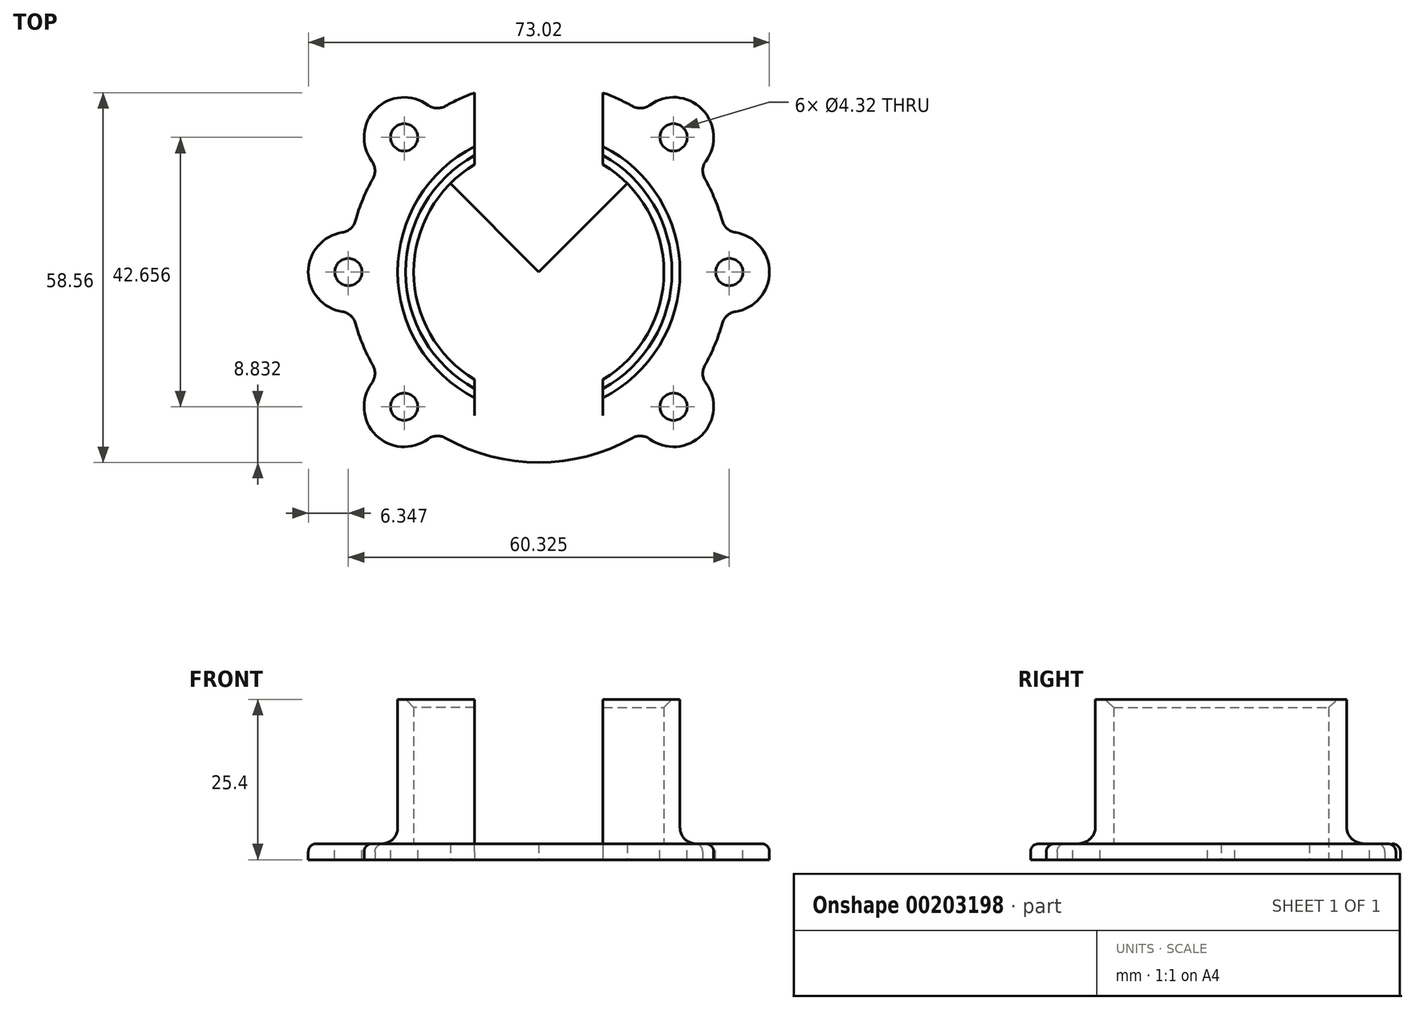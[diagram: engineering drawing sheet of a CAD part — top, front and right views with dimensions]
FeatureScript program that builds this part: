
annotation { "Feature Type Name" : "Feature", "Feature Type Description" : "" }
export const myFeature = defineFeature(function(context is Context, id is Id, definition is map)
    precondition{}
    {
        {
            var Q0;
            Q0=qCreatedBy(makeId("Top.planeOp"),FACE);
            var sketch = newSketch(context, id + "F0", { "sketchPlane" : qUnion([Q0])});
            skArc(sketch, "E0", {"start": v(-10.16, 17) * mm, "mid": v(-19.81, 0) * mm, "end": v(-10.16, -17) * mm});
            skArc(sketch, "E1.0", {"start": v(-10.16, 19.9) * mm, "mid": v(-22.35, 0) * mm, "end": v(-10.16, -19.9) * mm});
            skArc(sketch, "E2", {"start": v(-10.16, -36.72) * mm, "mid": v(0, -38.1) * mm, "end": v(10.16, -36.72) * mm});
            skArc(sketch, "E3", {"start": v(-26.28, 14.81) * mm, "mid": v(-27.87, 11.54) * mm, "end": v(-29.05, 8.1) * mm});
            skLineSegment(sketch, "E4", {"start": v(0, 0) * mm, "end": v(0, 38.1) * mm});
            skLineSegment(sketch, "E5", {"start": v(0, 38.1) * mm, "end": v(-10.16, 38.1) * mm});
            skLineSegment(sketch, "E6", {"start": v(-10.16, 38.1) * mm, "end": v(-10.16, 17) * mm});
            skLineSegment(sketch, "E7.MirrorCS", {"start": v(10.16, 38.1) * mm, "end": v(10.16, 17) * mm});
            skLineSegment(sketch, "E8.MirrorCS", {"start": v(0, 38.1) * mm, "end": v(10.16, 38.1) * mm});
            skLineSegment(sketch, "E9.MirrorCS", {"start": v(-10.16, -38.1) * mm, "end": v(-10.16, -17) * mm});
            skLineSegment(sketch, "E10.MirrorCS", {"start": v(10.16, -38.1) * mm, "end": v(10.16, -17) * mm});
            skArc(sketch, "E11.trimOffspring", {"start": v(10.16, -19.9) * mm, "mid": v(22.35, 0) * mm, "end": v(10.16, 19.9) * mm});
            skArc(sketch, "E12.trimOffspring", {"start": v(10.16, -17) * mm, "mid": v(19.81, 0) * mm, "end": v(10.16, 17) * mm});
            skLineSegment(sketch, "E13", {"start": v(-10.16, -38.1) * mm, "end": v(10.16, -38.1) * mm});
            skLineSegment(sketch, "E14", {"start": v(0, 0) * mm, "end": v(-30.16, 0) * mm});
            skLineSegment(sketch, "E15.1.0", {"start": v(0, 0) * mm, "end": v(-21.33, -21.33) * mm});
            skLineSegment(sketch, "E15.2.0", {"start": v(0, 0) * mm, "end": v(0, -30.16) * mm});
            skLineSegment(sketch, "E15.3.0", {"start": v(0, 0) * mm, "end": v(21.33, -21.33) * mm});
            skLineSegment(sketch, "E15.4.0", {"start": v(0, 0) * mm, "end": v(30.16, 0) * mm});
            skLineSegment(sketch, "E15.5.0", {"start": v(0, 0) * mm, "end": v(21.33, 21.33) * mm});
            skLineSegment(sketch, "E15.6.0", {"start": v(0, 0) * mm, "end": v(0, 30.16) * mm});
            skLineSegment(sketch, "E15.7.0", {"start": v(0, 0) * mm, "end": v(-21.33, 21.33) * mm});
            skArc(sketch, "E16", {"start": v(-31.12, 6.28) * mm, "mid": v(-36.51, 0) * mm, "end": v(-31.12, -6.28) * mm});
            skArc(sketch, "E17.1.0", {"start": v(-26.44, -17.56) * mm, "mid": v(-25.82, -25.82) * mm, "end": v(-17.56, -26.44) * mm});
            skArc(sketch, "E17.3.0", {"start": v(17.56, -26.44) * mm, "mid": v(25.82, -25.82) * mm, "end": v(26.44, -17.56) * mm});
            skArc(sketch, "E17.4.0", {"start": v(31.12, -6.28) * mm, "mid": v(36.51, 0) * mm, "end": v(31.12, 6.28) * mm});
            skArc(sketch, "E17.5.0", {"start": v(26.44, 17.56) * mm, "mid": v(25.82, 25.82) * mm, "end": v(17.56, 26.44) * mm});
            skArc(sketch, "E17.7.0", {"start": v(-17.56, 26.44) * mm, "mid": v(-25.82, 25.82) * mm, "end": v(-26.44, 17.56) * mm});
            skArc(sketch, "E18.trimOffspring", {"start": v(10.16, 36.72) * mm, "mid": v(0, 38.1) * mm, "end": v(-10.16, 36.72) * mm});
            skArc(sketch, "E19.trimOffspring", {"start": v(-29.05, -8.1) * mm, "mid": v(-27.87, -11.54) * mm, "end": v(-26.28, -14.81) * mm});
            skArc(sketch, "E20.trimOffspring", {"start": v(-14.81, -26.28) * mm, "mid": v(0, -30.16) * mm, "end": v(14.81, -26.28) * mm});
            skArc(sketch, "E21.trimOffspring", {"start": v(26.28, -14.81) * mm, "mid": v(27.87, -11.54) * mm, "end": v(29.05, -8.1) * mm});
            skArc(sketch, "E22.trimOffspring", {"start": v(29.05, 8.1) * mm, "mid": v(27.87, 11.54) * mm, "end": v(26.28, 14.81) * mm});
            skArc(sketch, "E23.trimOffspring", {"start": v(14.81, 26.28) * mm, "mid": v(0, 30.16) * mm, "end": v(-14.81, 26.28) * mm});
            skPoint(sketch, "E24.visualSharp", {"position": v(-16.4, 25.32) * mm});
            skArc(sketch, "E24.filletArc", {"start": v(-17.56, 26.44) * mm, "mid": v(-16.21, 25.95) * mm, "end": v(-14.81, 26.28) * mm});
            skPoint(sketch, "E25.visualSharp", {"position": v(-25.32, 16.4) * mm});
            skArc(sketch, "E25.filletArc", {"start": v(-26.28, 14.81) * mm, "mid": v(-25.95, 16.21) * mm, "end": v(-26.44, 17.56) * mm});
            skPoint(sketch, "E26.visualSharp", {"position": v(-29.5, 6.31) * mm});
            skArc(sketch, "E26.filletArc", {"start": v(-31.12, 6.28) * mm, "mid": v(-29.82, 6.89) * mm, "end": v(-29.05, 8.1) * mm});
            skPoint(sketch, "E27.visualSharp", {"position": v(-29.5, -6.31) * mm});
            skArc(sketch, "E27.filletArc", {"start": v(-29.05, -8.1) * mm, "mid": v(-29.82, -6.89) * mm, "end": v(-31.12, -6.28) * mm});
            skPoint(sketch, "E28.visualSharp", {"position": v(-25.32, -16.4) * mm});
            skArc(sketch, "E28.filletArc", {"start": v(-26.44, -17.56) * mm, "mid": v(-25.95, -16.21) * mm, "end": v(-26.28, -14.81) * mm});
            skPoint(sketch, "E29.visualSharp", {"position": v(-16.4, -25.32) * mm});
            skArc(sketch, "E29.filletArc", {"start": v(-14.81, -26.28) * mm, "mid": v(-16.21, -25.95) * mm, "end": v(-17.56, -26.44) * mm});
            skPoint(sketch, "E30.visualSharp", {"position": v(16.4, -25.32) * mm});
            skArc(sketch, "E30.filletArc", {"start": v(17.56, -26.44) * mm, "mid": v(16.21, -25.95) * mm, "end": v(14.81, -26.28) * mm});
            skPoint(sketch, "E31.visualSharp", {"position": v(25.32, -16.4) * mm});
            skArc(sketch, "E31.filletArc", {"start": v(26.28, -14.81) * mm, "mid": v(25.95, -16.21) * mm, "end": v(26.44, -17.56) * mm});
            skPoint(sketch, "E32.visualSharp", {"position": v(29.5, -6.31) * mm});
            skArc(sketch, "E32.filletArc", {"start": v(31.12, -6.28) * mm, "mid": v(29.82, -6.89) * mm, "end": v(29.05, -8.1) * mm});
            skPoint(sketch, "E33.visualSharp", {"position": v(29.5, 6.31) * mm});
            skArc(sketch, "E33.filletArc", {"start": v(29.05, 8.1) * mm, "mid": v(29.82, 6.89) * mm, "end": v(31.12, 6.28) * mm});
            skPoint(sketch, "E34.visualSharp", {"position": v(25.32, 16.4) * mm});
            skArc(sketch, "E34.filletArc", {"start": v(26.44, 17.56) * mm, "mid": v(25.95, 16.21) * mm, "end": v(26.28, 14.81) * mm});
            skPoint(sketch, "E35.visualSharp", {"position": v(16.4, 25.32) * mm});
            skArc(sketch, "E35.filletArc", {"start": v(14.81, 26.28) * mm, "mid": v(16.21, 25.95) * mm, "end": v(17.56, 26.44) * mm});
            skSolve(sketch);
        }
        {
            var Q0;
            {var subQ0=sQuery(id+"F0.wireOp",EDGE,"E15.6.0");Q0=makeQuery(id+"F0.imprint","IMPRINT",FACE,{"disambiguationData":[TD([[makeQuery(id+"F0.imprint","IMPRINT",EDGE,{"derivedFrom":subQ0}),1.0]])]});}
            var Q1;
            {var subQ0=sQuery(id+"F0.wireOp",EDGE,"E15.6.0");Q1=makeQuery(id+"F0.imprint","IMPRINT",FACE,{"disambiguationData":[TD([[makeQuery(id+"F0.imprint","IMPRINT",EDGE,{"derivedFrom":subQ0}),-1.0]])]});}
            var Q2;
            Q2=makeQuery(id+"F0.imprint","IMPRINT",FACE,{"disambiguationData":[TD([[makeQuery(id+"F0.imprint","IMPRINT",EDGE,{"derivedFrom":sQuery(id+"F0.wireOp",EDGE,"E17.3.0")}),1.0]])]});
            var Q3;
            Q3=makeQuery(id+"F0.imprint","IMPRINT",FACE,{"disambiguationData":[TD([[makeQuery(id+"F0.imprint","IMPRINT",EDGE,{"derivedFrom":sQuery(id+"F0.wireOp",EDGE,"E3")}),1.0]])]});
            var Q4;
            {var subQ0=sQuery(id+"F0.wireOp",EDGE,"E6");var subQ1=sQuery(id+"F0.wireOp",EDGE,"E0");var subQ2=makeQuery(id+"F0.imprint","INTERSECT",VERTEX,{"derivedFrom":[subQ1,subQ0]});Q4=makeQuery(id+"F0.imprint","IMPRINT",FACE,{"disambiguationData":[TD([[makeQuery(id+"F0.imprint","IMPRINT",EDGE,{"disambiguationData":[TD([[subQ2,-1.0]])],"derivedFrom":subQ1}),-1.0]])]});}
            var Q5;
            {var subQ0=sQuery(id+"F0.wireOp",EDGE,"E12.trimOffspring");var subQ1=sQuery(id+"F0.wireOp",EDGE,"E7.MirrorCS");var subQ2=makeQuery(id+"F0.imprint","INTERSECT",VERTEX,{"derivedFrom":[subQ1,subQ0]});Q5=makeQuery(id+"F0.imprint","IMPRINT",FACE,{"disambiguationData":[TD([[makeQuery(id+"F0.imprint","IMPRINT",EDGE,{"disambiguationData":[TD([[subQ2,1.0]])],"derivedFrom":subQ1}),1.0]])]});}
            var Q6;
            {var subQ0=sQuery(id+"F0.wireOp",EDGE,"E15.7.0");var subQ1=sQuery(id+"F0.wireOp",EDGE,"E0");var subQ2=makeQuery(id+"F0.imprint","INTERSECT",VERTEX,{"derivedFrom":[subQ1,subQ0]});Q6=makeQuery(id+"F0.imprint","IMPRINT",FACE,{"disambiguationData":[TD([[makeQuery(id+"F0.imprint","IMPRINT",EDGE,{"disambiguationData":[TD([[subQ2,-1.0]])],"derivedFrom":subQ1}),-1.0]])]});}
            var Q7;
            {var subQ0=sQuery(id+"F0.wireOp",EDGE,"E15.7.0");var subQ1=sQuery(id+"F0.wireOp",EDGE,"E0");var subQ2=makeQuery(id+"F0.imprint","INTERSECT",VERTEX,{"derivedFrom":[subQ1,subQ0]});Q7=makeQuery(id+"F0.imprint","IMPRINT",FACE,{"disambiguationData":[TD([[makeQuery(id+"F0.imprint","IMPRINT",EDGE,{"disambiguationData":[TD([[subQ2,-1.0]])],"derivedFrom":subQ1}),1.0]])]});}
            var Q8;
            {var subQ0=sQuery(id+"F0.wireOp",EDGE,"E14");var subQ1=sQuery(id+"F0.wireOp",EDGE,"E0");var subQ2=makeQuery(id+"F0.imprint","INTERSECT",VERTEX,{"derivedFrom":[subQ1,subQ0]});Q8=makeQuery(id+"F0.imprint","IMPRINT",FACE,{"disambiguationData":[TD([[makeQuery(id+"F0.imprint","IMPRINT",EDGE,{"disambiguationData":[TD([[subQ2,-1.0]])],"derivedFrom":subQ1}),-1.0]])]});}
            var Q9;
            {var subQ0=sQuery(id+"F0.wireOp",EDGE,"E14");var subQ1=sQuery(id+"F0.wireOp",EDGE,"E0");var subQ2=makeQuery(id+"F0.imprint","INTERSECT",VERTEX,{"derivedFrom":[subQ1,subQ0]});Q9=makeQuery(id+"F0.imprint","IMPRINT",FACE,{"disambiguationData":[TD([[makeQuery(id+"F0.imprint","IMPRINT",EDGE,{"disambiguationData":[TD([[subQ2,-1.0]])],"derivedFrom":subQ1}),1.0]])]});}
            var Q10;
            {var subQ0=sQuery(id+"F0.wireOp",EDGE,"E15.2.0");Q10=makeQuery(id+"F0.imprint","IMPRINT",FACE,{"disambiguationData":[TD([[makeQuery(id+"F0.imprint","IMPRINT",EDGE,{"derivedFrom":subQ0}),-1.0]])]});}
            var Q11;
            {var subQ6=sQuery(id+"F0.wireOp",EDGE,"E15.2.0");Q11=makeQuery(id+"F0.imprint","IMPRINT",FACE,{"disambiguationData":[TD([[makeQuery(id+"F0.imprint","IMPRINT",EDGE,{"derivedFrom":subQ6}),1.0]])]});}
            var Q12;
            {var subQ0=sQuery(id+"F0.wireOp",EDGE,"E15.3.0");var subQ1=sQuery(id+"F0.wireOp",EDGE,"E12.trimOffspring");var subQ2=makeQuery(id+"F0.imprint","INTERSECT",VERTEX,{"derivedFrom":[subQ1,subQ0]});Q12=makeQuery(id+"F0.imprint","IMPRINT",FACE,{"disambiguationData":[TD([[makeQuery(id+"F0.imprint","IMPRINT",EDGE,{"disambiguationData":[TD([[subQ2,-1.0]])],"derivedFrom":subQ1}),1.0]])]});}
            var Q13;
            {var subQ0=sQuery(id+"F0.wireOp",EDGE,"E15.4.0");var subQ1=sQuery(id+"F0.wireOp",EDGE,"E12.trimOffspring");var subQ2=makeQuery(id+"F0.imprint","INTERSECT",VERTEX,{"derivedFrom":[subQ1,subQ0]});Q13=makeQuery(id+"F0.imprint","IMPRINT",FACE,{"disambiguationData":[TD([[makeQuery(id+"F0.imprint","IMPRINT",EDGE,{"disambiguationData":[TD([[subQ2,-1.0]])],"derivedFrom":subQ1}),1.0]])]});}
            var Q14;
            {var subQ0=sQuery(id+"F0.wireOp",EDGE,"E15.4.0");var subQ1=sQuery(id+"F0.wireOp",EDGE,"E11.trimOffspring");var subQ2=makeQuery(id+"F0.imprint","INTERSECT",VERTEX,{"derivedFrom":[subQ1,subQ0]});Q14=makeQuery(id+"F0.imprint","IMPRINT",FACE,{"disambiguationData":[TD([[makeQuery(id+"F0.imprint","IMPRINT",EDGE,{"disambiguationData":[TD([[subQ2,-1.0]])],"derivedFrom":subQ1}),1.0]])]});}
            var Q15;
            {var subQ0=sQuery(id+"F0.wireOp",EDGE,"E15.3.0");var subQ1=sQuery(id+"F0.wireOp",EDGE,"E11.trimOffspring");var subQ2=makeQuery(id+"F0.imprint","INTERSECT",VERTEX,{"derivedFrom":[subQ1,subQ0]});Q15=makeQuery(id+"F0.imprint","IMPRINT",FACE,{"disambiguationData":[TD([[makeQuery(id+"F0.imprint","IMPRINT",EDGE,{"disambiguationData":[TD([[subQ2,-1.0]])],"derivedFrom":subQ1}),1.0]])]});}
            var Q16;
            {var subQ0=sQuery(id+"F0.wireOp",EDGE,"E12.trimOffspring");var subQ1=sQuery(id+"F0.wireOp",EDGE,"E10.MirrorCS");var subQ2=makeQuery(id+"F0.imprint","INTERSECT",VERTEX,{"derivedFrom":[subQ1,subQ0]});Q16=makeQuery(id+"F0.imprint","IMPRINT",FACE,{"disambiguationData":[TD([[makeQuery(id+"F0.imprint","IMPRINT",EDGE,{"disambiguationData":[TD([[subQ2,1.0]])],"derivedFrom":subQ1}),-1.0]])]});}
            var Q17;
            {var subQ0=sQuery(id+"F0.wireOp",EDGE,"E9.MirrorCS");var subQ1=sQuery(id+"F0.wireOp",EDGE,"E0");var subQ2=makeQuery(id+"F0.imprint","INTERSECT",VERTEX,{"derivedFrom":[subQ1,subQ0]});Q17=makeQuery(id+"F0.imprint","IMPRINT",FACE,{"disambiguationData":[TD([[makeQuery(id+"F0.imprint","IMPRINT",EDGE,{"disambiguationData":[TD([[subQ2,1.0]])],"derivedFrom":subQ1}),-1.0]])]});}
            extrude(context, id + "F1", {"entities" : qUnion([Q0, Q1, Q2, Q3, Q4, Q5, Q6, Q7, Q8, Q9, Q10, Q11, Q12, Q13, Q14, Q15, Q16, Q17]), "depth" : 2.54 * mm});
        }
        {
            var Q0;
            Q0=sQuery(id+"F0.wireOp",VERTEX,"E15.7.0.end");
            var Q1;
            Q1=sQuery(id+"F0.wireOp",VERTEX,"E14.end");
            var Q2;
            Q2=sQuery(id+"F0.wireOp",VERTEX,"E15.1.0.end");
            var Q3;
            Q3=sQuery(id+"F0.wireOp",VERTEX,"E17.3.0.center");
            var Q4;
            Q4=sQuery(id+"F0.wireOp",VERTEX,"E15.4.0.end");
            var Q5;
            Q5=sQuery(id+"F0.wireOp",VERTEX,"E15.5.0.end");
            var Q6;
            Q6=makeQuery(id+"F1.opExtrude","SWEPT_BODY",BODY,{"disambiguationData":[OSD([sQuery(id+"F0.wireOp",EDGE,"E3"),sQuery(id+"F0.wireOp",EDGE,"E16"),sQuery(id+"F0.wireOp",EDGE,"E17.1.0"),sQuery(id+"F0.wireOp",EDGE,"E17.3.0"),sQuery(id+"F0.wireOp",EDGE,"E17.4.0"),sQuery(id+"F0.wireOp",EDGE,"E17.5.0"),sQuery(id+"F0.wireOp",EDGE,"E17.7.0"),sQuery(id+"F0.wireOp",EDGE,"E19.trimOffspring"),sQuery(id+"F0.wireOp",EDGE,"E20.trimOffspring"),sQuery(id+"F0.wireOp",EDGE,"E21.trimOffspring"),sQuery(id+"F0.wireOp",EDGE,"E22.trimOffspring"),sQuery(id+"F0.wireOp",EDGE,"E23.trimOffspring"),sQuery(id+"F0.wireOp",EDGE,"E24.filletArc"),sQuery(id+"F0.wireOp",EDGE,"E25.filletArc"),sQuery(id+"F0.wireOp",EDGE,"E26.filletArc"),sQuery(id+"F0.wireOp",EDGE,"E27.filletArc"),sQuery(id+"F0.wireOp",EDGE,"E28.filletArc"),sQuery(id+"F0.wireOp",EDGE,"E29.filletArc"),sQuery(id+"F0.wireOp",EDGE,"E30.filletArc"),sQuery(id+"F0.wireOp",EDGE,"E31.filletArc"),sQuery(id+"F0.wireOp",EDGE,"E32.filletArc"),sQuery(id+"F0.wireOp",EDGE,"E33.filletArc"),sQuery(id+"F0.wireOp",EDGE,"E34.filletArc"),sQuery(id+"F0.wireOp",EDGE,"E35.filletArc")])]});
            hole(context, id + "F2", {"style" : HoleStyle.SIMPLE, "endStyle" : HoleEndStyle.BLIND, "oppositeDirection" : true, "standardTappedOrClearance" : lookupTablePath({ "standard" : "ANSI", "fit" : "Close", "size" : "#8", "type" : "Clearance" }), "standardBlindInLast" : lookupTablePath({ "fit" : "Close", "standard" : "ANSI", "size" : "#8", "type" : "Clearance" }), "holeDiameter" : 4.32 * mm, "holeDepth" : 25.4 * mm, "locations" : qUnion([Q0, Q1, Q2, Q3, Q4, Q5]), "scope" : qUnion([Q6])});
        }
        {
            var Q0;
            {var subQ0=sQuery(id+"F0.wireOp",EDGE,"E6");var subQ1=sQuery(id+"F0.wireOp",EDGE,"E0");var subQ2=makeQuery(id+"F0.imprint","INTERSECT",VERTEX,{"derivedFrom":[subQ1,subQ0]});Q0=makeQuery(id+"F0.imprint","IMPRINT",FACE,{"disambiguationData":[TD([[makeQuery(id+"F0.imprint","IMPRINT",EDGE,{"disambiguationData":[TD([[subQ2,-1.0]])],"derivedFrom":subQ1}),-1.0]])]});}
            var Q1;
            {var subQ0=sQuery(id+"F0.wireOp",EDGE,"E15.7.0");var subQ1=sQuery(id+"F0.wireOp",EDGE,"E0");var subQ2=makeQuery(id+"F0.imprint","INTERSECT",VERTEX,{"derivedFrom":[subQ1,subQ0]});Q1=makeQuery(id+"F0.imprint","IMPRINT",FACE,{"disambiguationData":[TD([[makeQuery(id+"F0.imprint","IMPRINT",EDGE,{"disambiguationData":[TD([[subQ2,-1.0]])],"derivedFrom":subQ1}),-1.0]])]});}
            var Q2;
            {var subQ0=sQuery(id+"F0.wireOp",EDGE,"E14");var subQ1=sQuery(id+"F0.wireOp",EDGE,"E0");var subQ2=makeQuery(id+"F0.imprint","INTERSECT",VERTEX,{"derivedFrom":[subQ1,subQ0]});Q2=makeQuery(id+"F0.imprint","IMPRINT",FACE,{"disambiguationData":[TD([[makeQuery(id+"F0.imprint","IMPRINT",EDGE,{"disambiguationData":[TD([[subQ2,-1.0]])],"derivedFrom":subQ1}),-1.0]])]});}
            var Q3;
            {var subQ0=sQuery(id+"F0.wireOp",EDGE,"E9.MirrorCS");var subQ1=sQuery(id+"F0.wireOp",EDGE,"E0");var subQ2=makeQuery(id+"F0.imprint","INTERSECT",VERTEX,{"derivedFrom":[subQ1,subQ0]});Q3=makeQuery(id+"F0.imprint","IMPRINT",FACE,{"disambiguationData":[TD([[makeQuery(id+"F0.imprint","IMPRINT",EDGE,{"disambiguationData":[TD([[subQ2,1.0]])],"derivedFrom":subQ1}),-1.0]])]});}
            var Q4;
            {var subQ0=sQuery(id+"F0.wireOp",EDGE,"E12.trimOffspring");var subQ1=sQuery(id+"F0.wireOp",EDGE,"E10.MirrorCS");var subQ2=makeQuery(id+"F0.imprint","INTERSECT",VERTEX,{"derivedFrom":[subQ1,subQ0]});Q4=makeQuery(id+"F0.imprint","IMPRINT",FACE,{"disambiguationData":[TD([[makeQuery(id+"F0.imprint","IMPRINT",EDGE,{"disambiguationData":[TD([[subQ2,1.0]])],"derivedFrom":subQ1}),-1.0]])]});}
            var Q5;
            {var subQ0=sQuery(id+"F0.wireOp",EDGE,"E15.3.0");var subQ1=sQuery(id+"F0.wireOp",EDGE,"E11.trimOffspring");var subQ2=makeQuery(id+"F0.imprint","INTERSECT",VERTEX,{"derivedFrom":[subQ1,subQ0]});Q5=makeQuery(id+"F0.imprint","IMPRINT",FACE,{"disambiguationData":[TD([[makeQuery(id+"F0.imprint","IMPRINT",EDGE,{"disambiguationData":[TD([[subQ2,-1.0]])],"derivedFrom":subQ1}),1.0]])]});}
            var Q6;
            {var subQ0=sQuery(id+"F0.wireOp",EDGE,"E15.4.0");var subQ1=sQuery(id+"F0.wireOp",EDGE,"E11.trimOffspring");var subQ2=makeQuery(id+"F0.imprint","INTERSECT",VERTEX,{"derivedFrom":[subQ1,subQ0]});Q6=makeQuery(id+"F0.imprint","IMPRINT",FACE,{"disambiguationData":[TD([[makeQuery(id+"F0.imprint","IMPRINT",EDGE,{"disambiguationData":[TD([[subQ2,-1.0]])],"derivedFrom":subQ1}),1.0]])]});}
            var Q7;
            {var subQ0=sQuery(id+"F0.wireOp",EDGE,"E12.trimOffspring");var subQ1=sQuery(id+"F0.wireOp",EDGE,"E7.MirrorCS");var subQ2=makeQuery(id+"F0.imprint","INTERSECT",VERTEX,{"derivedFrom":[subQ1,subQ0]});Q7=makeQuery(id+"F0.imprint","IMPRINT",FACE,{"disambiguationData":[TD([[makeQuery(id+"F0.imprint","IMPRINT",EDGE,{"disambiguationData":[TD([[subQ2,1.0]])],"derivedFrom":subQ1}),1.0]])]});}
            extrude(context, id + "F3", {"entities" : qUnion([Q0, Q1, Q2, Q3, Q4, Q5, Q6, Q7]), "operationType" : NewBodyOperationType.ADD, "depth" : 25.4 * mm});
        }
        {
            var Q0;
            Q0=makeQuery(id+"F3.boolean.opBoolean","INTERSECT",EDGE,{"derivedFrom":[makeQuery(id+"F1.opExtrude","CAP_FACE",FACE,{"disambiguationData":[OSD([sQuery(id+"F0.wireOp",EDGE,"E3"),sQuery(id+"F0.wireOp",EDGE,"E16"),sQuery(id+"F0.wireOp",EDGE,"E17.1.0"),sQuery(id+"F0.wireOp",EDGE,"E17.3.0"),sQuery(id+"F0.wireOp",EDGE,"E17.4.0"),sQuery(id+"F0.wireOp",EDGE,"E17.5.0"),sQuery(id+"F0.wireOp",EDGE,"E17.7.0"),sQuery(id+"F0.wireOp",EDGE,"E19.trimOffspring"),sQuery(id+"F0.wireOp",EDGE,"E20.trimOffspring"),sQuery(id+"F0.wireOp",EDGE,"E21.trimOffspring"),sQuery(id+"F0.wireOp",EDGE,"E22.trimOffspring"),sQuery(id+"F0.wireOp",EDGE,"E23.trimOffspring"),sQuery(id+"F0.wireOp",EDGE,"E24.filletArc"),sQuery(id+"F0.wireOp",EDGE,"E25.filletArc"),sQuery(id+"F0.wireOp",EDGE,"E26.filletArc"),sQuery(id+"F0.wireOp",EDGE,"E27.filletArc"),sQuery(id+"F0.wireOp",EDGE,"E28.filletArc"),sQuery(id+"F0.wireOp",EDGE,"E29.filletArc"),sQuery(id+"F0.wireOp",EDGE,"E30.filletArc"),sQuery(id+"F0.wireOp",EDGE,"E31.filletArc"),sQuery(id+"F0.wireOp",EDGE,"E32.filletArc"),sQuery(id+"F0.wireOp",EDGE,"E33.filletArc"),sQuery(id+"F0.wireOp",EDGE,"E34.filletArc"),sQuery(id+"F0.wireOp",EDGE,"E35.filletArc")])],"isStart":false}),makeQuery(id+"F3.opExtrude","SWEPT_FACE",FACE,{"disambiguationData":[OSD([sQuery(id+"F0.wireOp",EDGE,"E1.0")])]})]});
            var Q1;
            Q1=makeQuery(id+"F3.boolean.opBoolean","INTERSECT",EDGE,{"derivedFrom":[makeQuery(id+"F1.opExtrude","CAP_FACE",FACE,{"disambiguationData":[OSD([sQuery(id+"F0.wireOp",EDGE,"E3"),sQuery(id+"F0.wireOp",EDGE,"E16"),sQuery(id+"F0.wireOp",EDGE,"E17.1.0"),sQuery(id+"F0.wireOp",EDGE,"E17.3.0"),sQuery(id+"F0.wireOp",EDGE,"E17.4.0"),sQuery(id+"F0.wireOp",EDGE,"E17.5.0"),sQuery(id+"F0.wireOp",EDGE,"E17.7.0"),sQuery(id+"F0.wireOp",EDGE,"E19.trimOffspring"),sQuery(id+"F0.wireOp",EDGE,"E20.trimOffspring"),sQuery(id+"F0.wireOp",EDGE,"E21.trimOffspring"),sQuery(id+"F0.wireOp",EDGE,"E22.trimOffspring"),sQuery(id+"F0.wireOp",EDGE,"E23.trimOffspring"),sQuery(id+"F0.wireOp",EDGE,"E24.filletArc"),sQuery(id+"F0.wireOp",EDGE,"E25.filletArc"),sQuery(id+"F0.wireOp",EDGE,"E26.filletArc"),sQuery(id+"F0.wireOp",EDGE,"E27.filletArc"),sQuery(id+"F0.wireOp",EDGE,"E28.filletArc"),sQuery(id+"F0.wireOp",EDGE,"E29.filletArc"),sQuery(id+"F0.wireOp",EDGE,"E30.filletArc"),sQuery(id+"F0.wireOp",EDGE,"E31.filletArc"),sQuery(id+"F0.wireOp",EDGE,"E32.filletArc"),sQuery(id+"F0.wireOp",EDGE,"E33.filletArc"),sQuery(id+"F0.wireOp",EDGE,"E34.filletArc"),sQuery(id+"F0.wireOp",EDGE,"E35.filletArc")])],"isStart":false}),makeQuery(id+"F3.opExtrude","SWEPT_FACE",FACE,{"disambiguationData":[OSD([sQuery(id+"F0.wireOp",EDGE,"E11.trimOffspring")])]})]});
            fillet(context, id + "F4", {"entities" : qUnion([Q0, Q1]), "radius" : 2.54 * mm, "tangentPropagation" : true, "allowEdgeOverflow" : false});
        }
        {
            var Q0;
            Q0=makeQuery(id+"F3.opExtrude","CAP_EDGE",EDGE,{"disambiguationData":[OSD([sQuery(id+"F0.wireOp",EDGE,"E0")])],"isStart":false});
            var Q1;
            Q1=makeQuery(id+"F3.opExtrude","CAP_EDGE",EDGE,{"disambiguationData":[OSD([sQuery(id+"F0.wireOp",EDGE,"E12.trimOffspring")])],"isStart":false});
            chamfer(context, id + "F5", {"entities" : qUnion([Q0, Q1]), "width" : 1.27 * mm, "tangentPropagation" : true});
        }
        {
            var Q0;
            Q0=makeQuery(id+"F1.opExtrude","CAP_EDGE",EDGE,{"disambiguationData":[OSD([sQuery(id+"F0.wireOp",EDGE,"E17.1.0")])],"isStart":false});
            var Q1;
            Q1=makeQuery(id+"F1.opExtrude","CAP_EDGE",EDGE,{"disambiguationData":[OSD([sQuery(id+"F0.wireOp",EDGE,"E29.filletArc")])],"isStart":false});
            fillet(context, id + "F6", {"entities" : qUnion([Q0, Q1]), "radius" : 1.27 * mm, "tangentPropagation" : true, "allowEdgeOverflow" : false});
        }
    });
